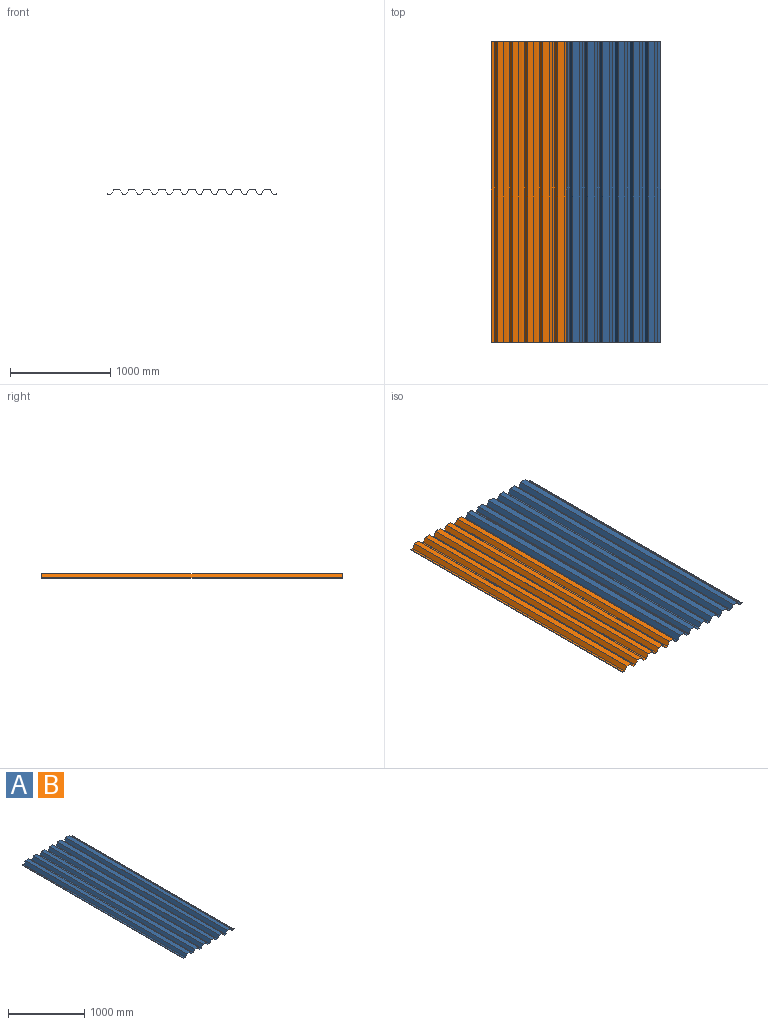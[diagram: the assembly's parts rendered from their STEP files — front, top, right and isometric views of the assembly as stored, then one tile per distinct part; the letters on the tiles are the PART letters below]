
ASSEMBLY  parts=2 mates=1
PART A: 58 faces, bbox 940.9x3000x46.5 mm
  f0: plane 3000x46mm, normal (-0.84,0,0.55), area 164754.4mm2, adj f1,f55,f56,f57
  f1: plane 3000x29.46mm, normal (0,0,1), area 88374.9mm2, adj f0,f2,f56,f57
  f2: plane 3000x8.15mm, normal (0.84,0,0.55), area 29187.5mm2, adj f1,f3,f56,f57
  f3: plane 3000x0.42mm, normal (-0.55,0,0.84), area 1500mm2, adj f2,f4,f56,f57
  f4: plane 3000x8.38mm, normal (-0.84,0,-0.55), area 30000mm2, adj f3,f5,f56,f57
  f5: plane 3000x30mm, normal (0,0,-1), area 90000mm2, adj f4,f6,f56,f57
  f6: plane 3000x46mm, normal (0.84,0,-0.55), area 164754.4mm2, adj f5,f7,f56,f57
  f7: plane 3000x60mm, normal (0,0,-1), area 180000mm2, adj f6,f8,f56,f57
  f8: plane 3000x46mm, normal (-0.84,0,-0.55), area 164754.4mm2, adj f7,f9,f56,f57
  f9: plane 3000x30mm, normal (0,0,-1), area 90000mm2, adj f8,f10,f56,f57
  f10: plane 3000x46mm, normal (0.84,0,-0.55), area 164754.4mm2, adj f9,f11,f56,f57
  f11: plane 3000x60mm, normal (0,0,-1), area 180000mm2, adj f10,f12,f56,f57
  f12: plane 3000x46mm, normal (-0.84,0,-0.55), area 164754.4mm2, adj f11,f13,f56,f57
  f13: plane 3000x30mm, normal (0,0,-1), area 90000mm2, adj f12,f14,f56,f57
  f14: plane 3000x46mm, normal (0.84,0,-0.55), area 164754.4mm2, adj f13,f15,f56,f57
  f15: plane 3000x60mm, normal (0,0,-1), area 180000mm2, adj f14,f16,f56,f57
  f16: plane 3000x46mm, normal (-0.84,0,-0.55), area 164754.4mm2, adj f15,f17,f56,f57
  f17: plane 3000x30mm, normal (0,0,-1), area 90000mm2, adj f16,f18,f56,f57
  f18: plane 3000x46mm, normal (0.84,0,-0.55), area 164754.4mm2, adj f17,f19,f56,f57
  f19: plane 3000x60mm, normal (0,0,-1), area 180000mm2, adj f18,f20,f56,f57
  f20: plane 3000x46mm, normal (-0.84,0,-0.55), area 164754.4mm2, adj f19,f21,f56,f57
  f21: plane 3000x30mm, normal (0,0,-1), area 90000mm2, adj f20,f22,f56,f57
  f22: plane 3000x46mm, normal (0.84,0,-0.55), area 164754.4mm2, adj f21,f23,f56,f57
  f23: plane 3000x60mm, normal (0,0,-1), area 180000mm2, adj f22,f24,f56,f57
  f24: plane 3000x46mm, normal (-0.84,0,-0.55), area 164754.4mm2, adj f23,f25,f56,f57
  f25: plane 3000x30mm, normal (0,0,-1), area 90000mm2, adj f24,f26,f56,f57
  f26: plane 3000x46mm, normal (0.84,0,-0.55), area 164754.4mm2, adj f25,f27,f56,f57
  f27: plane 3000x60mm, normal (0,0,-1), area 180000mm2, adj f26,f28,f56,f57
  f28: plane 3000x46mm, normal (-0.84,0,-0.55), area 164754.4mm2, adj f27,f29,f56,f57
  f29: plane 3000x30mm, normal (0,0,-1), area 90000mm2, adj f28,f30,f56,f57
  f30: plane 3000x8.38mm, normal (0.84,0,-0.55), area 30000mm2, adj f29,f31,f56,f57
  f31: plane 3000x0.42mm, normal (0.55,0,0.84), area 1500mm2, adj f30,f32,f56,f57
  f32: plane 3000x8.15mm, normal (-0.84,0,0.55), area 29187.5mm2, adj f31,f33,f56,f57
  f33: plane 3000x29.46mm, normal (0,0,1), area 88374.9mm2, adj f32,f34,f56,f57
  f34: plane 3000x46mm, normal (0.84,0,0.55), area 164754.4mm2, adj f33,f35,f56,f57
  f35: plane 3000x60.54mm, normal (0,0,1), area 181625.1mm2, adj f34,f36,f56,f57
  f36: plane 3000x46mm, normal (-0.84,0,0.55), area 164754.4mm2, adj f35,f37,f56,f57
  f37: plane 3000x29.46mm, normal (0,0,1), area 88374.9mm2, adj f36,f38,f56,f57
  f38: plane 3000x46mm, normal (0.84,0,0.55), area 164754.4mm2, adj f37,f39,f56,f57
  f39: plane 3000x60.54mm, normal (0,0,1), area 181625.1mm2, adj f38,f40,f56,f57
  f40: plane 3000x46mm, normal (-0.84,0,0.55), area 164754.4mm2, adj f39,f41,f56,f57
  f41: plane 3000x29.46mm, normal (0,0,1), area 88374.9mm2, adj f40,f42,f56,f57
  f42: plane 3000x46mm, normal (0.84,0,0.55), area 164754.4mm2, adj f41,f43,f56,f57
  f43: plane 3000x60.54mm, normal (0,0,1), area 181625.1mm2, adj f42,f44,f56,f57
  f44: plane 3000x46mm, normal (-0.84,0,0.55), area 164754.4mm2, adj f43,f45,f56,f57
  f45: plane 3000x29.46mm, normal (0,0,1), area 88374.9mm2, adj f44,f46,f56,f57
  f46: plane 3000x46mm, normal (0.84,0,0.55), area 164754.4mm2, adj f45,f47,f56,f57
  f47: plane 3000x60.54mm, normal (0,0,1), area 181625.1mm2, adj f46,f48,f56,f57
  f48: plane 3000x46mm, normal (-0.84,0,0.55), area 164754.4mm2, adj f47,f49,f56,f57
  f49: plane 3000x29.46mm, normal (0,0,1), area 88374.9mm2, adj f48,f50,f56,f57
  f50: plane 3000x46mm, normal (0.84,0,0.55), area 164754.4mm2, adj f49,f51,f56,f57
  f51: plane 3000x60.54mm, normal (0,0,1), area 181625.1mm2, adj f50,f52,f56,f57
  f52: plane 3000x46mm, normal (-0.84,0,0.55), area 164754.4mm2, adj f51,f53,f56,f57
  f53: plane 3000x29.46mm, normal (0,0,1), area 88374.9mm2, adj f52,f54,f56,f57
  f54: plane 3000x46mm, normal (0.84,0,0.55), area 164754.4mm2, adj f53,f55,f56,f57
  f55: plane 3000x60.54mm, normal (0,0,1), area 181625.1mm2, adj f0,f54,f56,f57
  f56: plane 940.93x46.5mm, normal (0,-1,0), area 624.2mm2, adj f0,f1,f2,f3,f4,f5,f6,f7
  f57: plane 940.93x46.5mm, normal (0,1,0), area 624.2mm2, adj f0,f1,f2,f3,f4,f5,f6,f7
PART B: same geometry as A
PLACE A t=(-38.88,401.1,292.24)mm
PLACE B t=(-788.88,401.1,291.74)mm
MATE fastened B.f35 <-> A.f7  axis (0,0,1) through (51.12,-1098.9,338.24)mm
